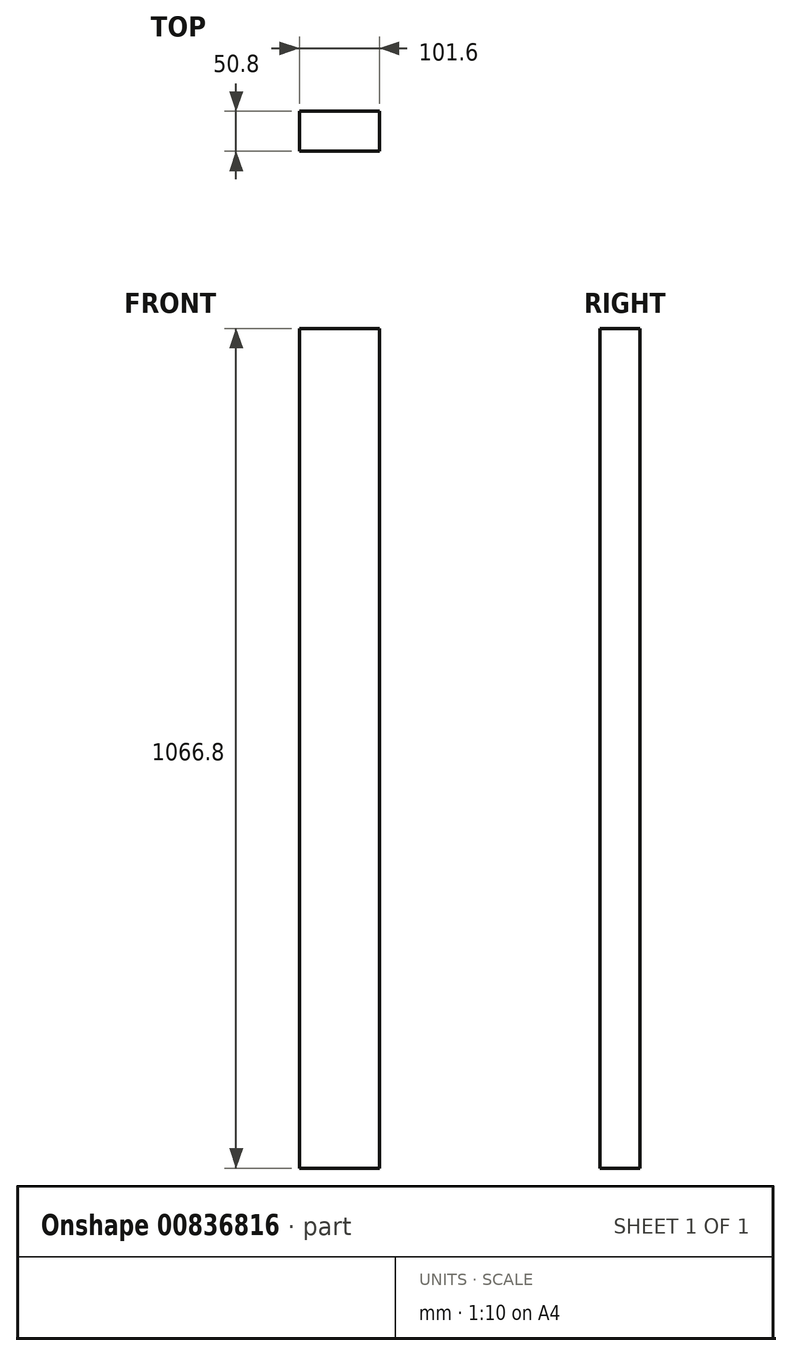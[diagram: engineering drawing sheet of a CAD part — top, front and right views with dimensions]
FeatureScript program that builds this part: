
annotation { "Feature Type Name" : "Feature", "Feature Type Description" : "" }
export const myFeature = defineFeature(function(context is Context, id is Id, definition is map)
    precondition{}
    {
        {
            var Q0;
            Q0=qCreatedBy(makeId("Right.planeOp"),FACE);
            var sketch = newSketch(context, id + "F0", { "sketchPlane" : qUnion([Q0])});
            skLineSegment(sketch, "E0.bottom", {"start": v(-89.3, 947.55) * mm, "end": v(-38.5, 947.55) * mm});
            skLineSegment(sketch, "E0.top", {"start": v(-89.3, -119.25) * mm, "end": v(-38.5, -119.25) * mm});
            skLineSegment(sketch, "E0.left", {"start": v(-89.3, 947.55) * mm, "end": v(-89.3, -119.25) * mm});
            skLineSegment(sketch, "E0.right", {"start": v(-38.5, 947.55) * mm, "end": v(-38.5, -119.25) * mm});
            skSolve(sketch);
        }
        {
            var Q0;
            Q0 = qSketchRegion(id + "F0", true);
            extrude(context, id + "F1", {"entities" : qUnion([Q0]), "depth" : 101.6 * mm, "offsetDistance" : 25.4 * mm});
        }
    });
